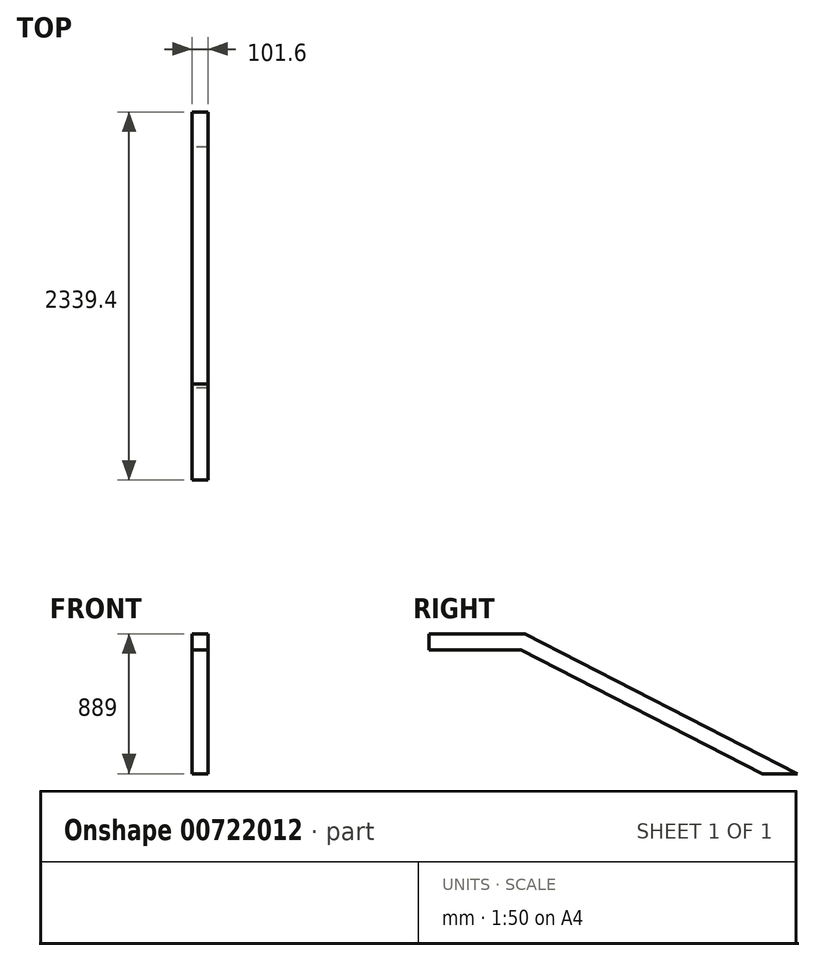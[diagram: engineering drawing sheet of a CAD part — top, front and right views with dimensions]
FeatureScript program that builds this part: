
annotation { "Feature Type Name" : "Feature", "Feature Type Description" : "" }
export const myFeature = defineFeature(function(context is Context, id is Id, definition is map)
    precondition{}
    {
        {
            var Q0;
            Q0=qCreatedBy(makeId("Right.planeOp"),FACE);
            var sketch = newSketch(context, id + "F0", { "sketchPlane" : qUnion([Q0])});
            skLineSegment(sketch, "E0.bottom", {"start": v(-48.3, 313.3) * mm, "end": v(561.3, 313.3) * mm});
            skLineSegment(sketch, "E0.top", {"start": v(-48.3, 211.7) * mm, "end": v(536.72, 211.7) * mm});
            skLineSegment(sketch, "E0.left", {"start": v(-48.3, 313.3) * mm, "end": v(-48.3, 211.7) * mm});
            skLineSegment(sketch, "E1", {"start": v(-48.3, 313.3) * mm, "end": v(-48.3, -575.7) * mm});
            skLineSegment(sketch, "E2", {"start": v(561.3, 313.3) * mm, "end": v(2291.1, -575.7) * mm});
            skLineSegment(sketch, "E3", {"start": v(2291.1, -575.7) * mm, "end": v(-48.3, -575.7) * mm});
            skLineSegment(sketch, "E4", {"start": v(536.72, 211.7) * mm, "end": v(2068.83, -575.7) * mm});
            skLineSegment(sketch, "E5.bottom", {"start": v(2085.3, -431.84) * mm, "end": v(2390.1, -431.84) * mm});
            skLineSegment(sketch, "E5.top", {"start": v(2085.3, -469.94) * mm, "end": v(2390.1, -469.94) * mm});
            skLineSegment(sketch, "E5.left", {"start": v(2085.3, -431.84) * mm, "end": v(2085.3, -469.94) * mm});
            skLineSegment(sketch, "E5.right", {"start": v(2390.1, -431.84) * mm, "end": v(2390.1, -469.94) * mm});
            skLineSegment(sketch, "E6", {"start": v(2068.83, -575.7) * mm, "end": v(2291.1, -575.7) * mm});
            skLineSegment(sketch, "E7.bottom", {"start": v(1780.5, -275.2) * mm, "end": v(2085.3, -275.2) * mm});
            skLineSegment(sketch, "E7.top", {"start": v(1780.5, -313.3) * mm, "end": v(2085.3, -313.3) * mm});
            skLineSegment(sketch, "E7.left", {"start": v(1780.5, -275.2) * mm, "end": v(1780.5, -313.3) * mm});
            skLineSegment(sketch, "E7.right", {"start": v(2085.3, -275.2) * mm, "end": v(2085.3, -313.3) * mm});
            skLineSegment(sketch, "E8.bottom", {"start": v(1475.7, -118.55) * mm, "end": v(1780.5, -118.55) * mm});
            skLineSegment(sketch, "E8.top", {"start": v(1475.7, -156.65) * mm, "end": v(1780.5, -156.65) * mm});
            skLineSegment(sketch, "E8.left", {"start": v(1475.7, -118.55) * mm, "end": v(1475.7, -156.65) * mm});
            skLineSegment(sketch, "E8.right", {"start": v(1780.5, -118.55) * mm, "end": v(1780.5, -156.65) * mm});
            skLineSegment(sketch, "E9.bottom", {"start": v(1170.9, 38.1) * mm, "end": v(1475.7, 38.1) * mm});
            skLineSegment(sketch, "E9.top", {"start": v(1170.9, 0) * mm, "end": v(1475.7, 0) * mm});
            skLineSegment(sketch, "E9.left", {"start": v(1170.9, 38.1) * mm, "end": v(1170.9, 0) * mm});
            skLineSegment(sketch, "E9.right", {"start": v(1475.7, 38.1) * mm, "end": v(1475.7, 0) * mm});
            skLineSegment(sketch, "E10.bottom", {"start": v(-48.3, 351.4) * mm, "end": v(866.1, 351.4) * mm});
            skLineSegment(sketch, "E10.top", {"start": v(-48.3, 313.3) * mm, "end": v(866.1, 313.3) * mm});
            skLineSegment(sketch, "E10.left", {"start": v(-48.3, 351.4) * mm, "end": v(-48.3, 313.3) * mm});
            skLineSegment(sketch, "E10.right", {"start": v(866.1, 351.4) * mm, "end": v(866.1, 313.3) * mm});
            skLineSegment(sketch, "E11.bottom", {"start": v(866.1, 194.75) * mm, "end": v(1170.9, 194.75) * mm});
            skLineSegment(sketch, "E11.top", {"start": v(866.1, 156.65) * mm, "end": v(1170.9, 156.65) * mm});
            skLineSegment(sketch, "E11.left", {"start": v(866.1, 194.75) * mm, "end": v(866.1, 156.65) * mm});
            skLineSegment(sketch, "E11.right", {"start": v(1170.9, 194.75) * mm, "end": v(1170.9, 156.65) * mm});
            skLineSegment(sketch, "E12", {"start": v(2390.1, -469.94) * mm, "end": v(2352, -469.94) * mm});
            skLineSegment(sketch, "E13", {"start": v(2352, -469.94) * mm, "end": v(2291.1, -575.7) * mm});
            skLineSegment(sketch, "E14", {"start": v(866.1, 313.3) * mm, "end": v(828, 313.3) * mm});
            skLineSegment(sketch, "E15", {"start": v(828, 313.3) * mm, "end": v(772.27, 204.86) * mm});
            skLineSegment(sketch, "E16", {"start": v(866.1, 313.3) * mm, "end": v(802.41, 189.38) * mm});
            skLineSegment(sketch, "E17", {"start": v(802.41, 189.38) * mm, "end": v(772.27, 204.86) * mm});
            skLineSegment(sketch, "E18", {"start": v(1170.9, 156.65) * mm, "end": v(1107.21, 32.73) * mm});
            skPoint(sketch, "E19.endSnap0", {"position": v(1426.2, -131.2) * mm});
            skLineSegment(sketch, "E20", {"start": v(1780.5, -156.65) * mm, "end": v(1716.81, -280.56) * mm});
            skLineSegment(sketch, "E21", {"start": v(2085.3, -313.3) * mm, "end": v(2021.61, -437.2) * mm});
            skLineSegment(sketch, "E22", {"start": v(2021.61, -437.2) * mm, "end": v(1987.72, -419.8) * mm});
            skLineSegment(sketch, "E23", {"start": v(1987.72, -419.8) * mm, "end": v(2042.46, -313.3) * mm});
            skLineSegment(sketch, "E24", {"start": v(2042.46, -313.3) * mm, "end": v(2085.3, -313.3) * mm});
            skLineSegment(sketch, "E25", {"start": v(1475.7, 0) * mm, "end": v(1412.01, -123.92) * mm});
            skSolve(sketch);
        }
        {
            var Q0;
            {var subQ1=sQuery(id+"F0.wireOp",EDGE,"E0.bottom");Q0=makeQuery(id+"F0.imprint","IMPRINT",FACE,{"disambiguationData":[TD([[makeQuery(id+"F0.imprint","IMPRINT",EDGE,{"derivedFrom":subQ1}),-1.0]])]});}
            var Q1;
            {var subQ10=sQuery(id+"F0.wireOp",EDGE,"E0.top");Q1=makeQuery(id+"F0.imprint","IMPRINT",FACE,{"disambiguationData":[TD([[makeQuery(id+"F0.imprint","IMPRINT",EDGE,{"derivedFrom":subQ10}),1.0]])]});}
            extrude(context, id + "F1", {"entities" : qUnion([Q0, Q1]), "depth" : 101.6 * mm, "offsetDistance" : 25.4 * mm});
        }
    });
